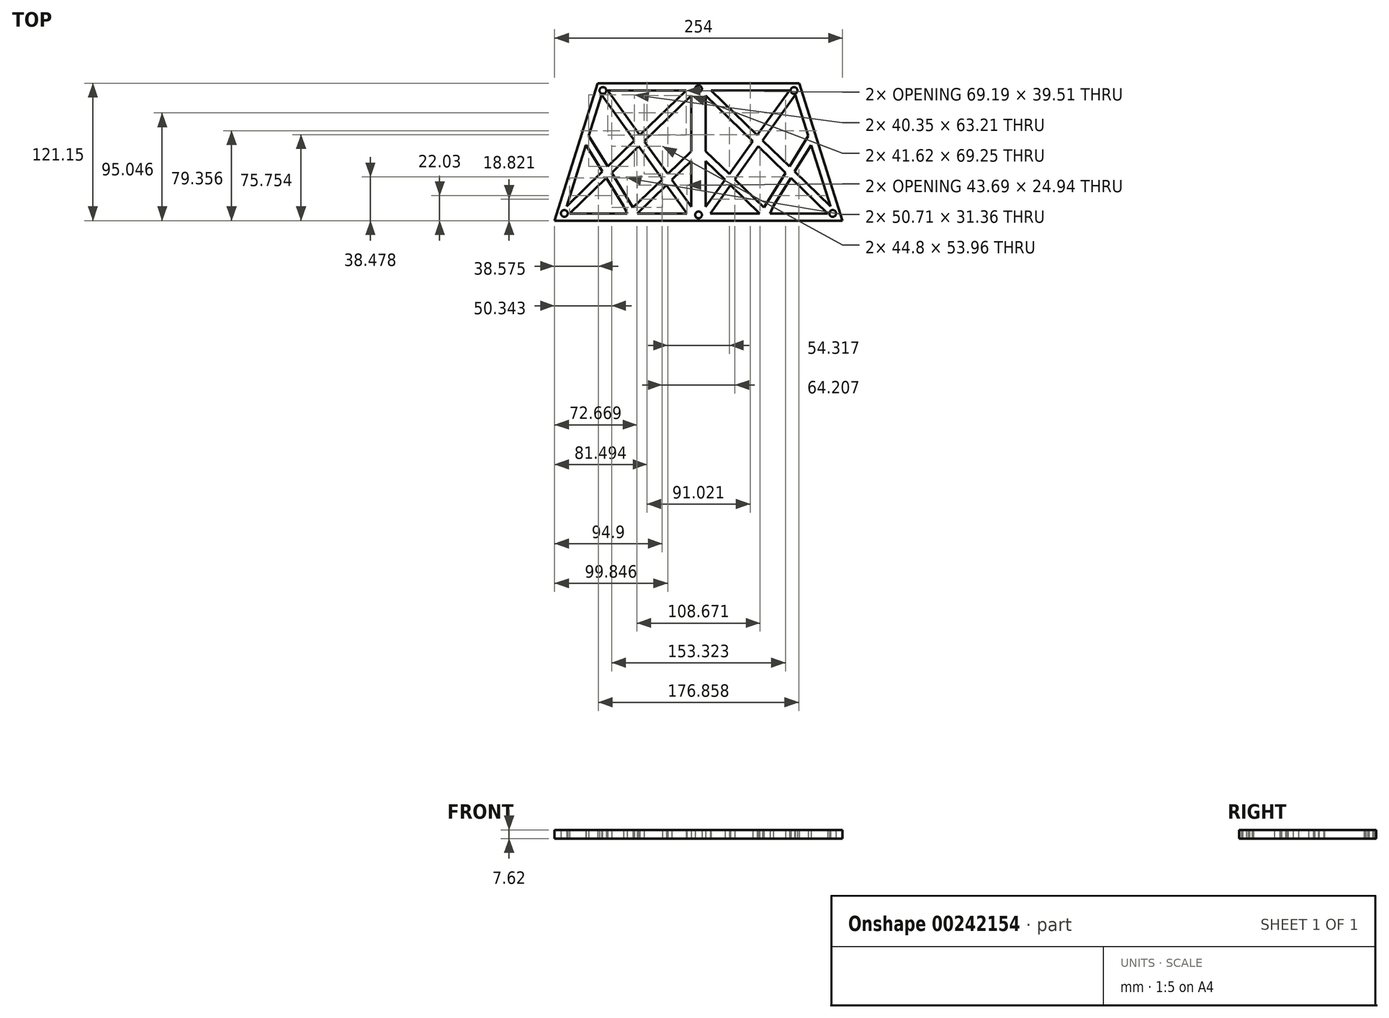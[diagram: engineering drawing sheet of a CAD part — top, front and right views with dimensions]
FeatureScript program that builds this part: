
annotation { "Feature Type Name" : "Feature", "Feature Type Description" : "" }
export const myFeature = defineFeature(function(context is Context, id is Id, definition is map)
    precondition{}
    {
        {
            var Q0;
            Q0=qCreatedBy(makeId("Top.planeOp"),FACE);
            var sketch = newSketch(context, id + "F0", { "sketchPlane" : qUnion([Q0])});
            skLineSegment(sketch, "E0", {"start": v(-113.47, -51.58) * mm, "end": v(13.53, -51.58) * mm});
            skLineSegment(sketch, "E1", {"start": v(13.53, 69.57) * mm, "end": v(-75.37, 69.57) * mm});
            skLineSegment(sketch, "E2", {"start": v(-75.37, 69.57) * mm, "end": v(-113.47, -51.58) * mm});
            skLineSegment(sketch, "E3", {"start": v(-85.85, 15.06) * mm, "end": v(-85.7, 15) * mm});
            skLineSegment(sketch, "E4", {"start": v(111.49, 19.62) * mm, "end": v(111.45, 19.6) * mm});
            skLineSegment(sketch, "E5", {"start": v(-71.91, 59.38) * mm, "end": v(-83.3, 23.17) * mm});
            skLineSegment(sketch, "E6", {"start": v(-100.25, -45.23) * mm, "end": v(-49.54, -45.23) * mm});
            skPoint(sketch, "E7.start.orphan", {"position": v(-62.83, 63.04) * mm});
            skPoint(sketch, "E8.start.orphan", {"position": v(-85.7, -51.58) * mm});
            skPoint(sketch, "E9.start.orphan", {"position": v(13.53, -45.23) * mm});
            skLineSegment(sketch, "E10", {"start": v(7.18, -39.4) * mm, "end": v(7.18, 0.86) * mm});
            skLineSegment(sketch, "E11.trimOffspring", {"start": v(2.62, 63.22) * mm, "end": v(-66.57, 63.22) * mm});
            skPoint(sketch, "E12.end.orphan", {"position": v(19.88, -33.06) * mm});
            skPoint(sketch, "E13.end.orphan", {"position": v(7.18, -33.06) * mm});
            skPoint(sketch, "E13.start.orphan", {"position": v(13.53, -33.06) * mm});
            skLineSegment(sketch, "E14", {"start": v(-71.91, 59.38) * mm, "end": v(-42.95, 19.09) * mm});
            skLineSegment(sketch, "E15", {"start": v(-66.57, 63.22) * mm, "end": v(-38.18, 23.71) * mm});
            skPoint(sketch, "E16.orphan", {"position": v(-70.76, 63.04) * mm});
            skPoint(sketch, "E17.orphan", {"position": v(-70.76, 63.22) * mm});
            skPoint(sketch, "E18.orphan", {"position": v(7.18, -45.23) * mm});
            skLineSegment(sketch, "E19", {"start": v(7.18, 58.8) * mm, "end": v(-34.43, 18.5) * mm});
            skLineSegment(sketch, "E20", {"start": v(2.62, 63.22) * mm, "end": v(-38.18, 23.71) * mm});
            skLineSegment(sketch, "E21.trimOffspring", {"start": v(-39.2, 13.88) * mm, "end": v(-18.4, -15.08) * mm});
            skLineSegment(sketch, "E22.trimOffspring", {"start": v(-42.95, 19.09) * mm, "end": v(-66.62, -3.83) * mm});
            skLineSegment(sketch, "E23.trimOffspring", {"start": v(-34.43, 18.5) * mm, "end": v(-13.62, -10.45) * mm});
            skLineSegment(sketch, "E24.trimOffspring", {"start": v(-39.2, 13.88) * mm, "end": v(-63.2, -9.36) * mm});
            skPoint(sketch, "E25.orphan", {"position": v(-104.81, -45.23) * mm});
            skLineSegment(sketch, "E26", {"start": v(-85.7, 15) * mm, "end": v(-71.28, -8.34) * mm});
            skLineSegment(sketch, "E27", {"start": v(-44.22, -40.08) * mm, "end": v(-63.2, -9.36) * mm});
            skLineSegment(sketch, "E28", {"start": v(-83.3, 23.17) * mm, "end": v(-66.62, -3.83) * mm});
            skLineSegment(sketch, "E29.trimOffspring", {"start": v(-40.41, -45.23) * mm, "end": v(3.27, -45.23) * mm});
            skLineSegment(sketch, "E30.trimOffspring", {"start": v(-67.86, -13.87) * mm, "end": v(-100.25, -45.23) * mm});
            skLineSegment(sketch, "E31.trimOffspring", {"start": v(-67.86, -13.87) * mm, "end": v(-52.49, -38.76) * mm});
            skLineSegment(sketch, "E32.trimOffspring", {"start": v(-71.28, -8.34) * mm, "end": v(-102.81, -38.88) * mm});
            skLineSegment(sketch, "E33.trimOffspring", {"start": v(-63.2, -9.36) * mm, "end": v(-44.22, -40.08) * mm});
            skPoint(sketch, "E34.endSnap0", {"position": v(7.18, 9.7) * mm});
            skPoint(sketch, "E35.trimOffspring.end.orphan", {"position": v(7.18, -5.22) * mm});
            skLineSegment(sketch, "E36", {"start": v(7.18, 9.7) * mm, "end": v(-13.62, -10.45) * mm});
            skLineSegment(sketch, "E37", {"start": v(-43.33, -39.22) * mm, "end": v(-44.22, -40.08) * mm});
            skPoint(sketch, "E38.orphan", {"position": v(-48.49, -45.23) * mm});
            skLineSegment(sketch, "E39", {"start": v(7.18, 0.86) * mm, "end": v(-9.88, -15.66) * mm});
            skPoint(sketch, "E40.trimOffspring.start.orphan", {"position": v(-43.33, -41.52) * mm});
            skPoint(sketch, "E41.orphan", {"position": v(-41.04, -45.23) * mm});
            skLineSegment(sketch, "E42.trimOffspring", {"start": v(7.18, 9.7) * mm, "end": v(7.18, 58.8) * mm});
            skLineSegment(sketch, "E43.trimOffspring", {"start": v(-9.88, -15.66) * mm, "end": v(7.18, -39.4) * mm});
            skLineSegment(sketch, "E44.trimOffspring", {"start": v(-18.4, -15.08) * mm, "end": v(-43.33, -39.22) * mm});
            skLineSegment(sketch, "E45.trimOffspring", {"start": v(-14.65, -20.29) * mm, "end": v(3.27, -45.23) * mm});
            skLineSegment(sketch, "E46.trimOffspring", {"start": v(-14.65, -20.29) * mm, "end": v(-40.41, -45.23) * mm});
            skLineSegment(sketch, "E47.trimOffspring", {"start": v(-66.62, -3.83) * mm, "end": v(-83.3, 23.17) * mm});
            skLineSegment(sketch, "E48.trimOffspring", {"start": v(-85.85, 15.06) * mm, "end": v(-102.81, -38.88) * mm});
            skLineSegment(sketch, "E49", {"start": v(-49.54, -45.23) * mm, "end": v(-52.49, -38.76) * mm});
            skPoint(sketch, "E50.end.orphan", {"position": v(102.43, 69.57) * mm});
            skPoint(sketch, "E51.orphan", {"position": v(140.53, -51.58) * mm});
            skPoint(sketch, "E52.trimOffspring.end.orphan", {"position": v(131.88, -45.23) * mm});
            skPoint(sketch, "E52.trimOffspring.start.orphan", {"position": v(19.88, -45.23) * mm});
            skLineSegment(sketch, "E53.MirrorCS", {"start": v(13.53, 69.57) * mm, "end": v(102.43, 69.57) * mm});
            skLineSegment(sketch, "E54.MirrorCS", {"start": v(24.45, 63.22) * mm, "end": v(93.64, 63.22) * mm});
            skLineSegment(sketch, "E55.MirrorCS", {"start": v(24.45, 63.22) * mm, "end": v(65.25, 23.71) * mm});
            skLineSegment(sketch, "E56.MirrorCS", {"start": v(19.88, 58.8) * mm, "end": v(61.5, 18.5) * mm});
            skLineSegment(sketch, "E57.MirrorCS", {"start": v(19.88, 9.7) * mm, "end": v(19.88, 58.8) * mm});
            skLineSegment(sketch, "E58.MirrorCS", {"start": v(19.88, 9.7) * mm, "end": v(40.7, -10.45) * mm});
            skLineSegment(sketch, "E59.MirrorCS", {"start": v(19.88, 0.86) * mm, "end": v(36.95, -15.66) * mm});
            skLineSegment(sketch, "E60.MirrorCS", {"start": v(36.95, -15.66) * mm, "end": v(19.88, -39.4) * mm});
            skLineSegment(sketch, "E61.MirrorCS", {"start": v(19.88, -39.4) * mm, "end": v(19.88, 0.86) * mm});
            skLineSegment(sketch, "E62.MirrorCS", {"start": v(41.72, -20.29) * mm, "end": v(23.8, -45.23) * mm});
            skLineSegment(sketch, "E63.MirrorCS", {"start": v(67.48, -45.23) * mm, "end": v(23.8, -45.23) * mm});
            skLineSegment(sketch, "E64.MirrorCS", {"start": v(140.53, -51.58) * mm, "end": v(13.53, -51.58) * mm});
            skLineSegment(sketch, "E65.MirrorCS", {"start": v(61.5, 18.5) * mm, "end": v(40.7, -10.45) * mm});
            skLineSegment(sketch, "E66.MirrorCS", {"start": v(66.28, 13.88) * mm, "end": v(45.47, -15.08) * mm});
            skLineSegment(sketch, "E67.MirrorCS", {"start": v(93.64, 63.22) * mm, "end": v(65.25, 23.71) * mm});
            skLineSegment(sketch, "E68.MirrorCS", {"start": v(102.43, 69.57) * mm, "end": v(140.53, -51.58) * mm});
            skLineSegment(sketch, "E69.MirrorCS", {"start": v(98.98, 59.38) * mm, "end": v(70.02, 19.09) * mm});
            skLineSegment(sketch, "E70.MirrorCS", {"start": v(93.69, -3.83) * mm, "end": v(110.37, 23.17) * mm});
            skLineSegment(sketch, "E71.MirrorCS", {"start": v(112.77, 15) * mm, "end": v(98.35, -8.34) * mm});
            skLineSegment(sketch, "E72.MirrorCS", {"start": v(70.02, 19.09) * mm, "end": v(93.69, -3.83) * mm});
            skLineSegment(sketch, "E73.MirrorCS", {"start": v(66.28, 13.88) * mm, "end": v(90.27, -9.36) * mm});
            skLineSegment(sketch, "E74.MirrorCS", {"start": v(71.3, -40.08) * mm, "end": v(90.27, -9.36) * mm});
            skLineSegment(sketch, "E75.MirrorCS", {"start": v(45.47, -15.08) * mm, "end": v(70.4, -39.22) * mm});
            skLineSegment(sketch, "E76.MirrorCS", {"start": v(41.72, -20.29) * mm, "end": v(67.48, -45.23) * mm});
            skLineSegment(sketch, "E77.MirrorCS", {"start": v(76.6, -45.23) * mm, "end": v(79.55, -38.76) * mm});
            skLineSegment(sketch, "E78.MirrorCS", {"start": v(94.93, -13.87) * mm, "end": v(79.55, -38.76) * mm});
            skLineSegment(sketch, "E79.MirrorCS", {"start": v(127.32, -45.23) * mm, "end": v(76.6, -45.23) * mm});
            skLineSegment(sketch, "E80.MirrorCS", {"start": v(94.93, -13.87) * mm, "end": v(127.32, -45.23) * mm});
            skLineSegment(sketch, "E81.MirrorCS", {"start": v(98.35, -8.34) * mm, "end": v(129.88, -38.88) * mm});
            skLineSegment(sketch, "E82.MirrorCS", {"start": v(98.98, 59.38) * mm, "end": v(110.37, 23.17) * mm});
            skLineSegment(sketch, "E83.MirrorCS", {"start": v(70.4, -39.22) * mm, "end": v(71.3, -40.08) * mm});
            skLineSegment(sketch, "E84", {"start": v(112.77, 15) * mm, "end": v(129.88, -38.88) * mm});
            skCircle(sketch, "E85", {"center": v(13.53, 64.71) * mm, "radius": 2.98 * mm});
            skCircle(sketch, "E86", {"center": v(13.53, -46.56) * mm, "radius": 2.98 * mm});
            skCircle(sketch, "E87", {"center": v(131.88, -45.23) * mm, "radius": 2.98 * mm});
            skPoint(sketch, "E88.center.orphan", {"position": v(-105.5, -46.56) * mm});
            skPoint(sketch, "E89.center.orphan", {"position": v(-71.94, 64.71) * mm});
            skPoint(sketch, "E90.center.orphan", {"position": v(98.85, 64.71) * mm});
            skCircle(sketch, "E91", {"center": v(-104.81, -45.23) * mm, "radius": 2.98 * mm});
            skCircle(sketch, "E92", {"center": v(-70.76, 63.22) * mm, "radius": 2.98 * mm});
            skPoint(sketch, "E93.orphan", {"position": v(97.3, 64.71) * mm});
            skCircle(sketch, "E94", {"center": v(97.77, 63.22) * mm, "radius": 2.98 * mm});
            skSolve(sketch);
        }
        {
            var Q0;
            Q0=makeQuery(id+"F0.imprint","IMPRINT",FACE,{"disambiguationData":[TD([[makeQuery(id+"F0.imprint","IMPRINT",EDGE,{"derivedFrom":sQuery(id+"F0.wireOp",EDGE,"E0")}),1.0]])]});
            extrude(context, id + "F1", {"entities" : qUnion([Q0]), "depth" : 7.62 * mm});
        }
    });
